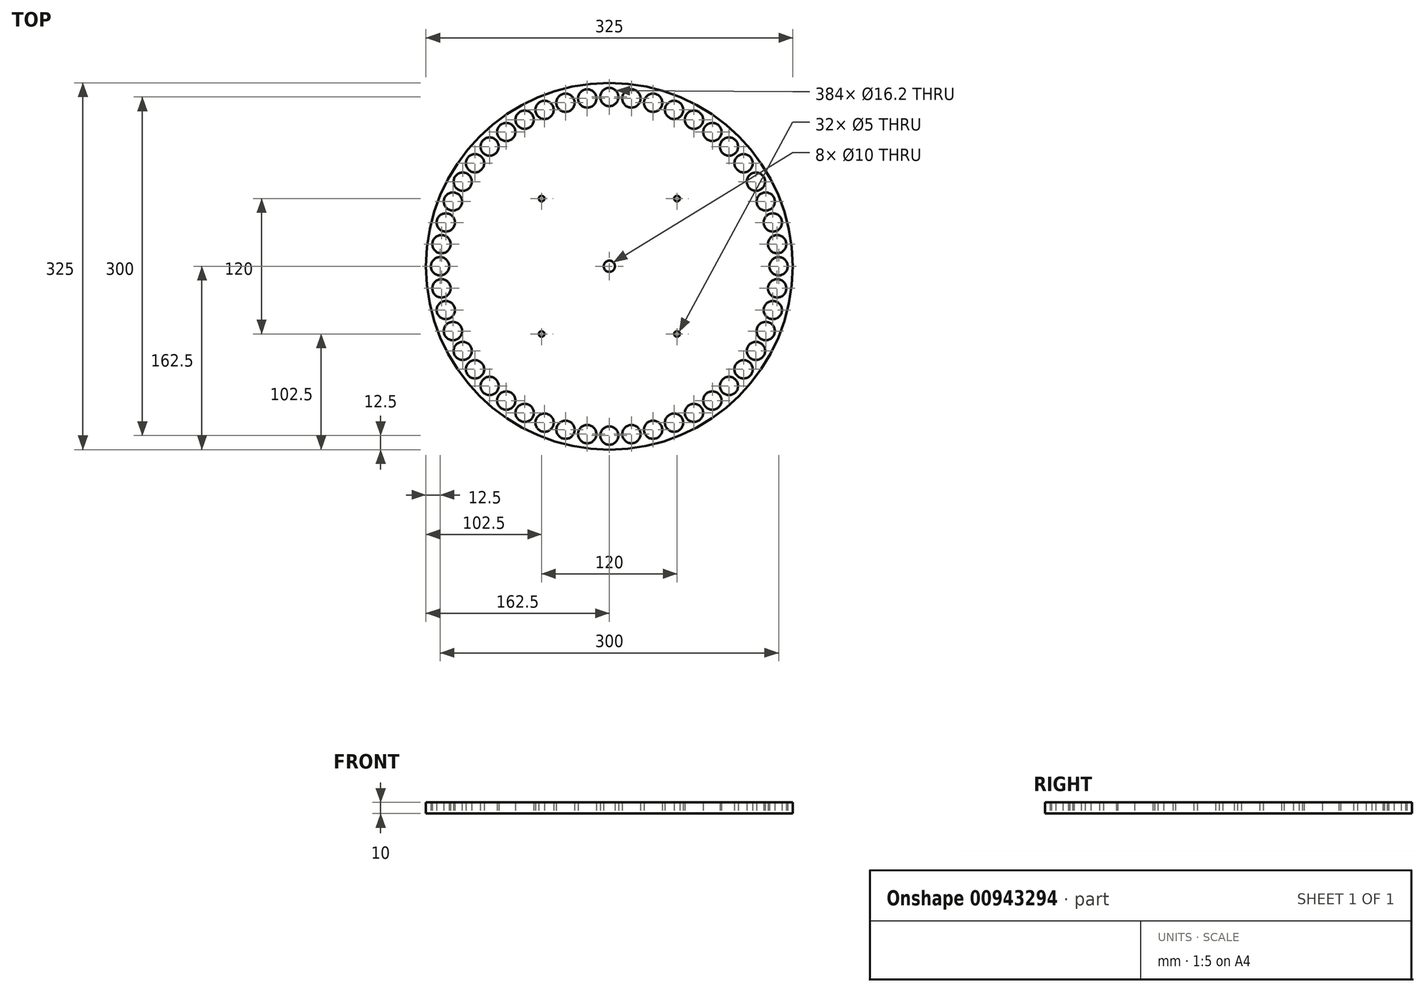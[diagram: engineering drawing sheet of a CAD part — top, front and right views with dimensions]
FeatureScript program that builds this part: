
annotation { "Feature Type Name" : "Feature", "Feature Type Description" : "" }
export const myFeature = defineFeature(function(context is Context, id is Id, definition is map)
    precondition{}
    {
        {
            var Q0;
            Q0=qCreatedBy(makeId("Top.planeOp"),FACE);
            var sketch = newSketch(context, id + "F0", { "sketchPlane" : qUnion([Q0])});
            skCircle(sketch, "E0", {"center": v(0, 0) * mm, "radius": 162.5 * mm});
            skCircle(sketch, "E1", {"center": v(0, 0) * mm, "radius": 150 * mm, "construction": true});
            skCircle(sketch, "E2", {"center": v(0, 150) * mm, "radius": 8.1 * mm});
            skLineSegment(sketch, "E3", {"start": v(0, 162.5) * mm, "end": v(0, -162.5) * mm, "construction": true});
            skLineSegment(sketch, "E4", {"start": v(-162.5, 0) * mm, "end": v(162.5, 0) * mm, "construction": true});
            skLineSegment(sketch, "E5", {"start": v(114.9, 114.9) * mm, "end": v(-114.9, -114.9) * mm, "construction": true});
            skLineSegment(sketch, "E6", {"start": v(-114.9, 114.9) * mm, "end": v(114.9, -114.9) * mm, "construction": true});
            skCircle(sketch, "E7.1.0", {"center": v(-19.58, 148.72) * mm, "radius": 8.1 * mm});
            skCircle(sketch, "E7.2.0", {"center": v(-38.82, 144.89) * mm, "radius": 8.1 * mm});
            skCircle(sketch, "E7.3.0", {"center": v(-57.4, 138.58) * mm, "radius": 8.1 * mm});
            skCircle(sketch, "E7.4.0", {"center": v(-75, 129.9) * mm, "radius": 8.1 * mm});
            skCircle(sketch, "E7.5.0", {"center": v(-91.31, 119) * mm, "radius": 8.1 * mm});
            skCircle(sketch, "E7.6.0", {"center": v(-106.07, 106.07) * mm, "radius": 8.1 * mm});
            skCircle(sketch, "E7.7.0", {"center": v(-119, 91.31) * mm, "radius": 8.1 * mm});
            skCircle(sketch, "E7.8.0", {"center": v(-129.9, 75) * mm, "radius": 8.1 * mm});
            skCircle(sketch, "E7.9.0", {"center": v(-138.58, 57.4) * mm, "radius": 8.1 * mm});
            skCircle(sketch, "E7.10.0", {"center": v(-144.89, 38.82) * mm, "radius": 8.1 * mm});
            skCircle(sketch, "E7.11.0", {"center": v(-148.72, 19.58) * mm, "radius": 8.1 * mm});
            skCircle(sketch, "E7.12.0", {"center": v(-150, 0) * mm, "radius": 8.1 * mm});
            skCircle(sketch, "E7.13.0", {"center": v(-148.72, -19.58) * mm, "radius": 8.1 * mm});
            skCircle(sketch, "E7.14.0", {"center": v(-144.89, -38.82) * mm, "radius": 8.1 * mm});
            skCircle(sketch, "E7.15.0", {"center": v(-138.58, -57.4) * mm, "radius": 8.1 * mm});
            skCircle(sketch, "E7.16.0", {"center": v(-129.9, -75) * mm, "radius": 8.1 * mm});
            skCircle(sketch, "E7.17.0", {"center": v(-119, -91.31) * mm, "radius": 8.1 * mm});
            skCircle(sketch, "E7.18.0", {"center": v(-106.07, -106.07) * mm, "radius": 8.1 * mm});
            skCircle(sketch, "E7.19.0", {"center": v(-91.31, -119) * mm, "radius": 8.1 * mm});
            skCircle(sketch, "E7.20.0", {"center": v(-75, -129.9) * mm, "radius": 8.1 * mm});
            skCircle(sketch, "E7.21.0", {"center": v(-57.4, -138.58) * mm, "radius": 8.1 * mm});
            skCircle(sketch, "E7.22.0", {"center": v(-38.82, -144.89) * mm, "radius": 8.1 * mm});
            skCircle(sketch, "E7.23.0", {"center": v(-19.58, -148.72) * mm, "radius": 8.1 * mm});
            skCircle(sketch, "E7.24.0", {"center": v(0, -150) * mm, "radius": 8.1 * mm});
            skCircle(sketch, "E7.25.0", {"center": v(19.58, -148.72) * mm, "radius": 8.1 * mm});
            skCircle(sketch, "E7.26.0", {"center": v(38.82, -144.89) * mm, "radius": 8.1 * mm});
            skCircle(sketch, "E7.27.0", {"center": v(57.4, -138.58) * mm, "radius": 8.1 * mm});
            skCircle(sketch, "E7.28.0", {"center": v(75, -129.9) * mm, "radius": 8.1 * mm});
            skCircle(sketch, "E7.29.0", {"center": v(91.31, -119) * mm, "radius": 8.1 * mm});
            skCircle(sketch, "E7.30.0", {"center": v(106.07, -106.07) * mm, "radius": 8.1 * mm});
            skCircle(sketch, "E7.31.0", {"center": v(119, -91.31) * mm, "radius": 8.1 * mm});
            skCircle(sketch, "E7.32.0", {"center": v(129.9, -75) * mm, "radius": 8.1 * mm});
            skCircle(sketch, "E7.33.0", {"center": v(138.58, -57.4) * mm, "radius": 8.1 * mm});
            skCircle(sketch, "E7.34.0", {"center": v(144.89, -38.82) * mm, "radius": 8.1 * mm});
            skCircle(sketch, "E7.35.0", {"center": v(148.72, -19.58) * mm, "radius": 8.1 * mm});
            skCircle(sketch, "E7.36.0", {"center": v(150, 0) * mm, "radius": 8.1 * mm});
            skCircle(sketch, "E7.37.0", {"center": v(148.72, 19.58) * mm, "radius": 8.1 * mm});
            skCircle(sketch, "E7.38.0", {"center": v(144.89, 38.82) * mm, "radius": 8.1 * mm});
            skCircle(sketch, "E7.39.0", {"center": v(138.58, 57.4) * mm, "radius": 8.1 * mm});
            skCircle(sketch, "E7.40.0", {"center": v(129.9, 75) * mm, "radius": 8.1 * mm});
            skCircle(sketch, "E7.41.0", {"center": v(119, 91.31) * mm, "radius": 8.1 * mm});
            skCircle(sketch, "E7.42.0", {"center": v(106.07, 106.07) * mm, "radius": 8.1 * mm});
            skCircle(sketch, "E7.43.0", {"center": v(91.31, 119) * mm, "radius": 8.1 * mm});
            skCircle(sketch, "E7.44.0", {"center": v(75, 129.9) * mm, "radius": 8.1 * mm});
            skCircle(sketch, "E7.45.0", {"center": v(57.4, 138.58) * mm, "radius": 8.1 * mm});
            skCircle(sketch, "E7.46.0", {"center": v(38.82, 144.89) * mm, "radius": 8.1 * mm});
            skCircle(sketch, "E7.47.0", {"center": v(19.58, 148.72) * mm, "radius": 8.1 * mm});
            skLineSegment(sketch, "E8.bottom", {"start": v(60, 60) * mm, "end": v(-60, 60) * mm, "construction": true});
            skLineSegment(sketch, "E8.top", {"start": v(60, -60) * mm, "end": v(-60, -60) * mm, "construction": true});
            skLineSegment(sketch, "E8.left", {"start": v(60, 60) * mm, "end": v(60, -60) * mm, "construction": true});
            skLineSegment(sketch, "E8.right", {"start": v(-60, 60) * mm, "end": v(-60, -60) * mm, "construction": true});
            skCircle(sketch, "E9", {"center": v(60, 60) * mm, "radius": 2.5 * mm});
            skCircle(sketch, "E10", {"center": v(60, -60) * mm, "radius": 2.5 * mm});
            skCircle(sketch, "E11", {"center": v(-60, -60) * mm, "radius": 2.5 * mm});
            skCircle(sketch, "E12", {"center": v(-60, 60) * mm, "radius": 2.5 * mm});
            skCircle(sketch, "E13", {"center": v(0, 0) * mm, "radius": 5 * mm});
            skSolve(sketch);
        }
        {
            var Q0;
            Q0=makeQuery(id+"F0.imprint","IMPRINT",FACE,{"disambiguationData":[TD([[makeQuery(id+"F0.imprint","IMPRINT",EDGE,{"derivedFrom":sQuery(id+"F0.wireOp",EDGE,"E0")}),1.0]])]});
            extrude(context, id + "F1", {"entities" : qUnion([Q0]), "depth" : 10 * mm, "offsetDistance" : 25 * mm});
        }
    });
